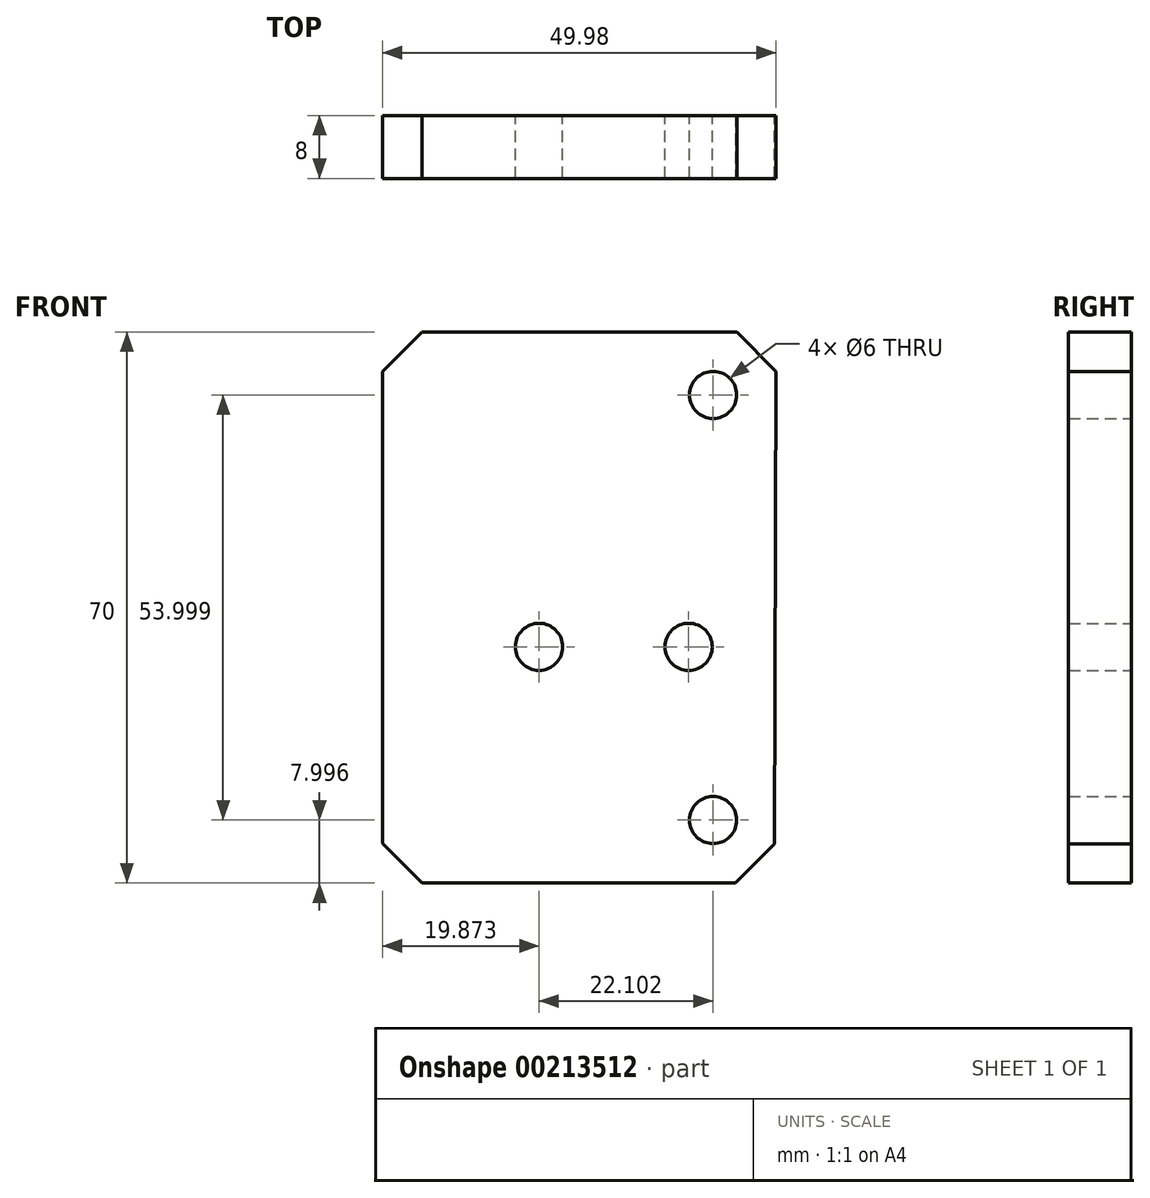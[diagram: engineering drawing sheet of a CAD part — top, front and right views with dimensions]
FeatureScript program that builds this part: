
annotation { "Feature Type Name" : "Feature", "Feature Type Description" : "" }
export const myFeature = defineFeature(function(context is Context, id is Id, definition is map)
    precondition{}
    {
        {
            var Q0;
            Q0=qCreatedBy(makeId("Front.planeOp"),FACE);
            var sketch = newSketch(context, id + "F0", { "sketchPlane" : qUnion([Q0])});
            skLineSegment(sketch, "E0.bottom", {"start": v(-24.82, 45) * mm, "end": v(25.18, 45) * mm});
            skLineSegment(sketch, "E0.top", {"start": v(-24.82, -25) * mm, "end": v(24.96, -25) * mm});
            skLineSegment(sketch, "E0.left", {"start": v(-24.82, 45) * mm, "end": v(-24.82, -25) * mm});
            skCircle(sketch, "E1", {"center": v(17.15, 37) * mm, "radius": 3 * mm});
            skLineSegment(sketch, "E2", {"start": v(-24.82, 10) * mm, "end": v(35.05, 10) * mm, "construction": true});
            skCircle(sketch, "E3.MirrorC", {"center": v(17.15, -17) * mm, "radius": 3 * mm});
            skCircle(sketch, "E4", {"center": v(-4.95, 5) * mm, "radius": 3 * mm});
            skCircle(sketch, "E5", {"center": v(14.05, 5) * mm, "radius": 3 * mm});
            skLineSegment(sketch, "E6", {"start": v(25.18, 45) * mm, "end": v(24.96, -25) * mm});
            skSolve(sketch);
        }
        {
            var Q0;
            Q0=qSketchRegion(id+"F0",true);
            extrude(context, id + "F1", {"entities" : qUnion([Q0]), "depth" : 8 * mm});
        }
        {
            var Q0;
            Q0=makeQuery(id+"F1.opExtrude","SWEPT_EDGE",EDGE,{"disambiguationData":[OSD([sQuery(id+"F0.wireOp",EDGE,"E0.bottom"),sQuery(id+"F0.wireOp",EDGE,"E6")])]});
            var Q1;
            Q1=makeQuery(id+"F1.opExtrude","SWEPT_EDGE",EDGE,{"disambiguationData":[OSD([sQuery(id+"F0.wireOp",EDGE,"E0.top"),sQuery(id+"F0.wireOp",EDGE,"E6")])]});
            var Q2;
            Q2=makeQuery(id+"F1.opExtrude","SWEPT_EDGE",EDGE,{"disambiguationData":[OSD([sQuery(id+"F0.wireOp",EDGE,"E0.bottom"),sQuery(id+"F0.wireOp",EDGE,"E0.left")])]});
            var Q3;
            Q3=makeQuery(id+"F1.opExtrude","SWEPT_EDGE",EDGE,{"disambiguationData":[OSD([sQuery(id+"F0.wireOp",EDGE,"E0.top"),sQuery(id+"F0.wireOp",EDGE,"E0.left")])]});
            chamfer(context, id + "F2", {"entities" : qUnion([Q0, Q1, Q2, Q3]), "width" : 5 * mm, "tangentPropagation" : true});
        }
    });
